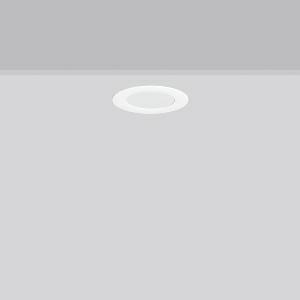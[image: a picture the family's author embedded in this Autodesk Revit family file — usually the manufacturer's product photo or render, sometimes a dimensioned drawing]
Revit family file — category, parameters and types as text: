
# Revit family: toledo_flat_round_e_901451_002_4028
name_source: partatom
category: Lighting Fixtures
units: mm (PartAtom-declared; Revit-internal decimal feet)

## family parameters
Cut with Voids When Loaded = No
Host = Face
Light Source = No
Part Type = Normal
Room Calculation Point = No
Round Connector Dimension = Use Diameter
Shared = No

## types (1)
- TOLEDO FLAT round E (1 x LED Modul 830, 470 lm, 3000)
    Apparent Load = 5 VA
    CIE Flux Codes = 48 79 96 100 100
    Color Rendering = 80
    Color Temperature = 3000
    Default Elevation = 1800 mm
    Description = Series: TOLEDO FLAT round
Ultra thin recessed downlight. Housing: die-cast aluminium. Light guide and diffuser made of non-yellowing PMMA, opal matt. Ceiling installation with spring system. Mounting depth depends on ceiling strength. Including separate LED converter with connecting cable 250 mm. Suitable for through-wiring with separately available accessories. Surface mounted housing as accessory for all sizes. Retrofittable decorative cylinders made of chintz fabric as accessory, optional with satin finish plastic diffuser. Through-wiring box (5 pole) available as accessory. 
Colour: white
Diameter: 148 mm
Height: 2 mm
Cut-out diameter: 128 mm
Recess height: 27-53 mm
Luminaire: recess height: 31-51 mm
Lamp: LED
Socket: without socket
Colour temperature: 3000K
Colour rendering index (CRI): 80
System power: 5 W
Rated luminous flux: 470 lm
Luminous efficiency: 94 lm/W
Control gear: Regulated power supply
Protection class: II
Type of protection: IP 54
    Height = 0 mm  [stored 0 ft]
    Lamp = 1 x LED Modul 830
    Lamp Light Flux = 470 lm
    Lamp count = 1
    Length = 148 mm
    Lifetime = 50000 h
    Luminous efficacy = 94 lm/W
    Manufacturer = RZB
    ModVariant = No
    Model = 901451.002
    Mounting Place = Ceiling
    Mounting Type = Recessed
    Number of Poles = 1
    OnlyDefault = Yes
    Power Factor = 1
    Product Name = TOLEDO FLAT round E
    Product group = Recessed downlights
    ProductGroupID = 402
    Protection Class = Protection class II
    Protection Degree = IP 20
    RLX_Detail_Level = 1
    RLX_Emergency_Light_Flux = 0 lm
    RLX_Emergency_Type = 0
    RLX_Emergency_Type_DB = No
    RlxData = <blob elided: 75165 chars, md5=26a9ac26>
    Socket = socket
    Standby Power = 0 W
    System Light Flux = 470 lm
    System Power = 5 W
    Type Comments = Product without accessories
    Type Image = 901451.002.jpg
    URL = http://relux.com
    VarID = ---
    Voltage = 230 V
    Voltage Range = 220-240 V
    Weight = 0.00 kg
    Width = 0 mm  [stored 0 ft]

note: [stored X ft] marks values corroborated as IEEE doubles in the binary element streams (Revit-internal decimal feet)

## geometry (parser evidence)
native form markers: Blend x4, Sweep x10
no freeform markers — native parametric forms only
